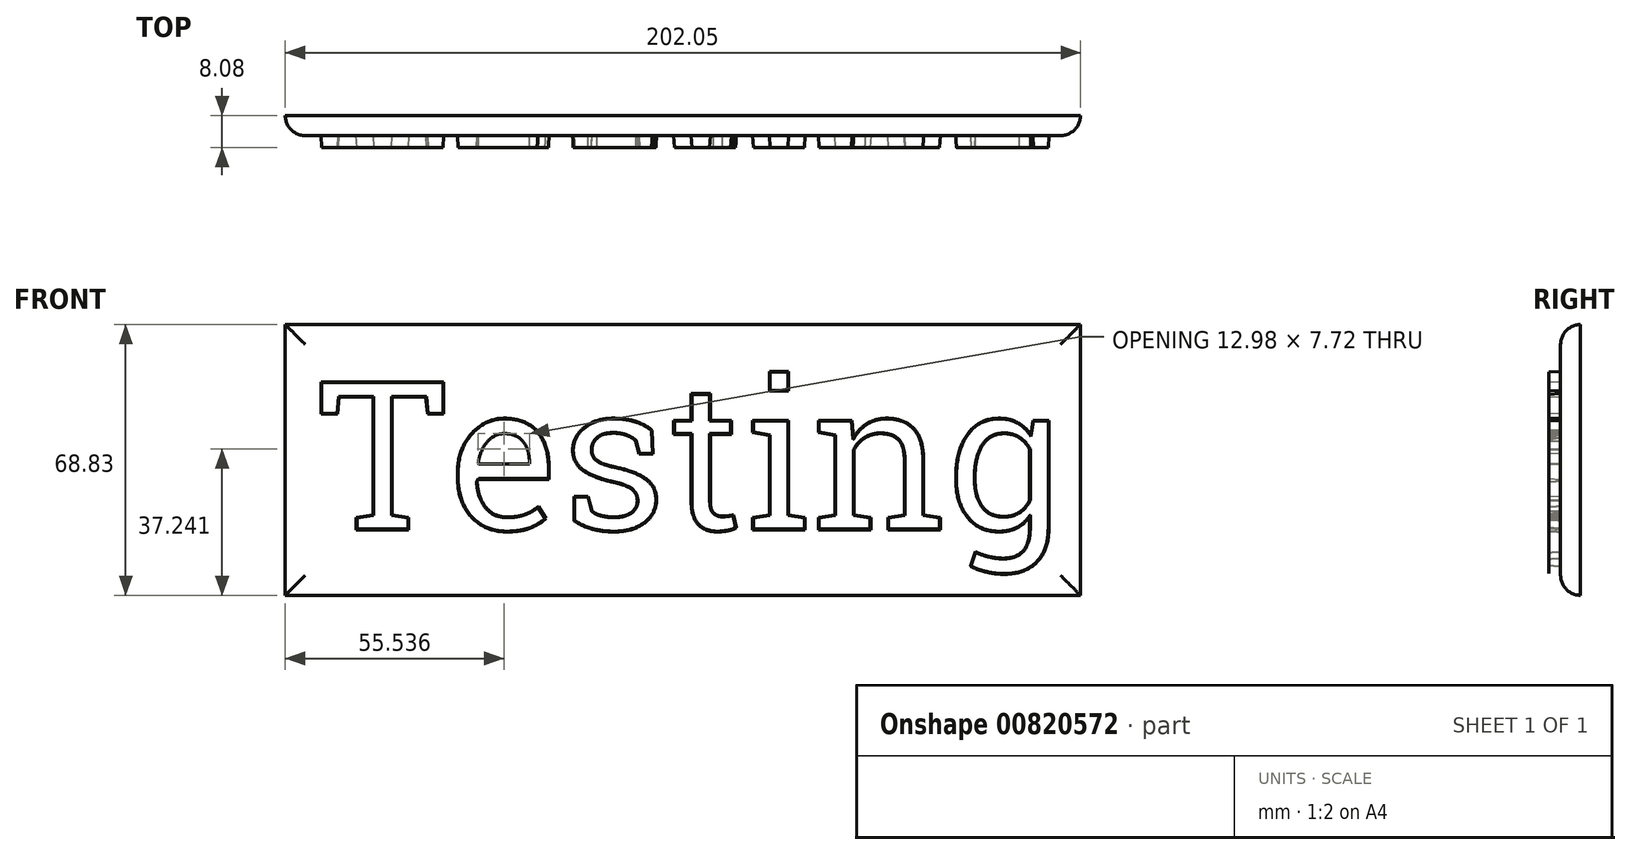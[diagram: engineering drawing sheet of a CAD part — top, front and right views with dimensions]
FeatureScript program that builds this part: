
annotation { "Feature Type Name" : "Feature", "Feature Type Description" : "" }
export const myFeature = defineFeature(function(context is Context, id is Id, definition is map)
    precondition{}
    {
        {
            var Q0;
            Q0=qCreatedBy(makeId("Front.planeOp"),FACE);
            var sketch = newSketch(context, id + "F0", { "sketchPlane" : qUnion([Q0])});
            skText(sketch, "E0", { "text": "Testing\n", "fontName": "RobotoSlab-Regular.ttf"});
            const initialGuessF0  = {"E0": [-0.06018, 0.01037, 1, 0, 0.0382]};
            skSetInitialGuess(sketch, initialGuessF0);
            skSolve(sketch);
        }
        {
            var Q0;
            Q0 = qSketchRegion(id + "F0", true);
            extrude(context, id + "F1", {"entities" : qUnion([Q0]), "depth" : 3 * mm, "offsetDistance" : 25.4 * mm});
        }
        {
            var Q0;
            Q0=qCreatedBy(makeId("Front.planeOp"),FACE);
            var sketch = newSketch(context, id + "F2", { "sketchPlane" : qUnion([Q0])});
            skLineSegment(sketch, "E1.bottom", {"start": v(-68.24, 62.63) * mm, "end": v(133.8, 62.63) * mm});
            skLineSegment(sketch, "E1.top", {"start": v(-68.24, -6.2) * mm, "end": v(133.8, -6.2) * mm});
            skLineSegment(sketch, "E1.left", {"start": v(-68.24, 62.63) * mm, "end": v(-68.24, -6.2) * mm});
            skLineSegment(sketch, "E1.right", {"start": v(133.8, 62.63) * mm, "end": v(133.8, -6.2) * mm});
            skSolve(sketch);
        }
        {
            var Q0;
            Q0 = qSketchRegion(id + "F2", true);
            extrude(context, id + "F3", {"entities" : qUnion([Q0]), "depth" : -5.08 * mm, "offsetDistance" : 25.4 * mm});
        }
        {
            var Q0;
            Q0=makeQuery(id+"F3.opExtrude","CAP_EDGE",EDGE,{"disambiguationData":[OSD([sQuery(id+"F2.wireOp",EDGE,"E1.left")])],"isStart":true});
            var Q1;
            Q1=makeQuery(id+"F3.opExtrude","CAP_EDGE",EDGE,{"disambiguationData":[OSD([sQuery(id+"F2.wireOp",EDGE,"E1.bottom")])],"isStart":true});
            var Q2;
            Q2=makeQuery(id+"F3.opExtrude","CAP_EDGE",EDGE,{"disambiguationData":[OSD([sQuery(id+"F2.wireOp",EDGE,"E1.right")])],"isStart":true});
            var Q3;
            Q3=makeQuery(id+"F3.opExtrude","CAP_EDGE",EDGE,{"disambiguationData":[OSD([sQuery(id+"F2.wireOp",EDGE,"E1.top")])],"isStart":true});
            chamfer(context, id + "F4", {"entities" : qUnion([Q0, Q1, Q2, Q3]), "chamferType" : ChamferType.OFFSET_ANGLE, "width" : 5.08 * mm, "oppositeDirection" : true, "angle" : 3 * degree, "tangentPropagation" : true});
        }
        {
            var Q0;
            Q0=makeQuery(id+"F1.opExtrude","CAP_EDGE",EDGE,{"disambiguationData":[OSD([sQuery(id+"F0.wireOp",EDGE,"E0.sketch_text.stroke-6")])],"isStart":false});
            var Q1;
            Q1=makeQuery(id+"F1.opExtrude","CAP_EDGE",EDGE,{"disambiguationData":[OSD([sQuery(id+"F0.wireOp",EDGE,"E0.sketch_text.stroke-7")])],"isStart":false});
            var Q2;
            Q2=makeQuery(id+"F1.opExtrude","CAP_EDGE",EDGE,{"disambiguationData":[OSD([sQuery(id+"F0.wireOp",EDGE,"E0.sketch_text.stroke-8")])],"isStart":false});
            var Q3;
            Q3=makeQuery(id+"F1.opExtrude","CAP_EDGE",EDGE,{"disambiguationData":[OSD([sQuery(id+"F0.wireOp",EDGE,"E0.sketch_text.stroke-9")])],"isStart":false});
            var Q4;
            Q4=makeQuery(id+"F1.opExtrude","CAP_EDGE",EDGE,{"disambiguationData":[OSD([sQuery(id+"F0.wireOp",EDGE,"E0.sketch_text.stroke-10")])],"isStart":false});
            var Q5;
            Q5=makeQuery(id+"F1.opExtrude","CAP_EDGE",EDGE,{"disambiguationData":[OSD([sQuery(id+"F0.wireOp",EDGE,"E0.sketch_text.stroke-5")])],"isStart":false});
            var Q6;
            Q6=makeQuery(id+"F1.opExtrude","CAP_EDGE",EDGE,{"disambiguationData":[OSD([sQuery(id+"F0.wireOp",EDGE,"E0.sketch_text.stroke-4")])],"isStart":false});
            var Q7;
            Q7=makeQuery(id+"F1.opExtrude","CAP_EDGE",EDGE,{"disambiguationData":[OSD([sQuery(id+"F0.wireOp",EDGE,"E0.sketch_text.stroke-3")])],"isStart":false});
            var Q8;
            Q8=makeQuery(id+"F1.opExtrude","CAP_EDGE",EDGE,{"disambiguationData":[OSD([sQuery(id+"F0.wireOp",EDGE,"E0.sketch_text.stroke-2")])],"isStart":false});
            var Q9;
            Q9=makeQuery(id+"F1.opExtrude","CAP_EDGE",EDGE,{"disambiguationData":[OSD([sQuery(id+"F0.wireOp",EDGE,"E0.sketch_text.stroke-1")])],"isStart":false});
            var Q10;
            Q10=makeQuery(id+"F1.opExtrude","CAP_EDGE",EDGE,{"disambiguationData":[OSD([sQuery(id+"F0.wireOp",EDGE,"E0.sketch_text.stroke-0")])],"isStart":false});
            var Q11;
            Q11=makeQuery(id+"F1.opExtrude","CAP_EDGE",EDGE,{"disambiguationData":[OSD([sQuery(id+"F0.wireOp",EDGE,"E0.sketch_text.stroke-15")])],"isStart":false});
            var Q12;
            Q12=makeQuery(id+"F1.opExtrude","CAP_EDGE",EDGE,{"disambiguationData":[OSD([sQuery(id+"F0.wireOp",EDGE,"E0.sketch_text.stroke-14")])],"isStart":false});
            var Q13;
            Q13=makeQuery(id+"F1.opExtrude","CAP_EDGE",EDGE,{"disambiguationData":[OSD([sQuery(id+"F0.wireOp",EDGE,"E0.sketch_text.stroke-13")])],"isStart":false});
            var Q14;
            Q14=makeQuery(id+"F1.opExtrude","CAP_EDGE",EDGE,{"disambiguationData":[OSD([sQuery(id+"F0.wireOp",EDGE,"E0.sketch_text.stroke-12")])],"isStart":false});
            var Q15;
            Q15=makeQuery(id+"F1.opExtrude","CAP_EDGE",EDGE,{"disambiguationData":[OSD([sQuery(id+"F0.wireOp",EDGE,"E0.sketch_text.stroke-11")])],"isStart":false});
            var Q16;
            Q16=makeQuery(id+"F1.opExtrude","CAP_EDGE",EDGE,{"disambiguationData":[OSD([sQuery(id+"F0.wireOp",EDGE,"E0.sketch_text.stroke-20")])],"isStart":false});
            var Q17;
            Q17=makeQuery(id+"F1.opExtrude","CAP_EDGE",EDGE,{"disambiguationData":[OSD([sQuery(id+"F0.wireOp",EDGE,"E0.sketch_text.stroke-21")])],"isStart":false});
            var Q18;
            Q18=makeQuery(id+"F1.opExtrude","CAP_EDGE",EDGE,{"disambiguationData":[OSD([sQuery(id+"F0.wireOp",EDGE,"E0.sketch_text.stroke-23")])],"isStart":false});
            var Q19;
            Q19=makeQuery(id+"F1.opExtrude","CAP_EDGE",EDGE,{"disambiguationData":[OSD([sQuery(id+"F0.wireOp",EDGE,"E0.sketch_text.stroke-24")])],"isStart":false});
            var Q20;
            Q20=makeQuery(id+"F1.opExtrude","CAP_EDGE",EDGE,{"disambiguationData":[OSD([sQuery(id+"F0.wireOp",EDGE,"E0.sketch_text.stroke-26")])],"isStart":false});
            var Q21;
            Q21=makeQuery(id+"F1.opExtrude","CAP_EDGE",EDGE,{"disambiguationData":[OSD([sQuery(id+"F0.wireOp",EDGE,"E0.sketch_text.stroke-27")])],"isStart":false});
            var Q22;
            Q22=makeQuery(id+"F1.opExtrude","CAP_EDGE",EDGE,{"disambiguationData":[OSD([sQuery(id+"F0.wireOp",EDGE,"E0.sketch_text.stroke-28")])],"isStart":false});
            var Q23;
            Q23=makeQuery(id+"F1.opExtrude","CAP_EDGE",EDGE,{"disambiguationData":[OSD([sQuery(id+"F0.wireOp",EDGE,"E0.sketch_text.stroke-29")])],"isStart":false});
            var Q24;
            Q24=makeQuery(id+"F1.opExtrude","CAP_EDGE",EDGE,{"disambiguationData":[OSD([sQuery(id+"F0.wireOp",EDGE,"E0.sketch_text.stroke-30")])],"isStart":false});
            var Q25;
            Q25=makeQuery(id+"F1.opExtrude","CAP_EDGE",EDGE,{"disambiguationData":[OSD([sQuery(id+"F0.wireOp",EDGE,"E0.sketch_text.stroke-31")])],"isStart":false});
            var Q26;
            Q26=makeQuery(id+"F1.opExtrude","CAP_EDGE",EDGE,{"disambiguationData":[OSD([sQuery(id+"F0.wireOp",EDGE,"E0.sketch_text.stroke-32")])],"isStart":false});
            var Q27;
            Q27=makeQuery(id+"F1.opExtrude","CAP_EDGE",EDGE,{"disambiguationData":[OSD([sQuery(id+"F0.wireOp",EDGE,"E0.sketch_text.stroke-16")])],"isStart":false});
            var Q28;
            Q28=makeQuery(id+"F1.opExtrude","CAP_EDGE",EDGE,{"disambiguationData":[OSD([sQuery(id+"F0.wireOp",EDGE,"E0.sketch_text.stroke-18")])],"isStart":false});
            var Q29;
            Q29=makeQuery(id+"F1.opExtrude","CAP_EDGE",EDGE,{"disambiguationData":[OSD([sQuery(id+"F0.wireOp",EDGE,"E0.sketch_text.stroke-17")])],"isStart":false});
            var Q30;
            Q30=makeQuery(id+"F1.opExtrude","CAP_EDGE",EDGE,{"disambiguationData":[OSD([sQuery(id+"F0.wireOp",EDGE,"E0.sketch_text.stroke-19")])],"isStart":false});
            var Q31;
            Q31=makeQuery(id+"F1.opExtrude","CAP_EDGE",EDGE,{"disambiguationData":[OSD([sQuery(id+"F0.wireOp",EDGE,"E0.sketch_text.stroke-55")])],"isStart":false});
            var Q32;
            Q32=makeQuery(id+"F1.opExtrude","CAP_EDGE",EDGE,{"disambiguationData":[OSD([sQuery(id+"F0.wireOp",EDGE,"E0.sketch_text.stroke-54")])],"isStart":false});
            var Q33;
            Q33=makeQuery(id+"F1.opExtrude","CAP_EDGE",EDGE,{"disambiguationData":[OSD([sQuery(id+"F0.wireOp",EDGE,"E0.sketch_text.stroke-53")])],"isStart":false});
            var Q34;
            Q34=makeQuery(id+"F1.opExtrude","CAP_EDGE",EDGE,{"disambiguationData":[OSD([sQuery(id+"F0.wireOp",EDGE,"E0.sketch_text.stroke-52")])],"isStart":false});
            var Q35;
            Q35=makeQuery(id+"F1.opExtrude","CAP_EDGE",EDGE,{"disambiguationData":[OSD([sQuery(id+"F0.wireOp",EDGE,"E0.sketch_text.stroke-51")])],"isStart":false});
            var Q36;
            Q36=makeQuery(id+"F1.opExtrude","CAP_EDGE",EDGE,{"disambiguationData":[OSD([sQuery(id+"F0.wireOp",EDGE,"E0.sketch_text.stroke-50")])],"isStart":false});
            var Q37;
            Q37=makeQuery(id+"F1.opExtrude","CAP_EDGE",EDGE,{"disambiguationData":[OSD([sQuery(id+"F0.wireOp",EDGE,"E0.sketch_text.stroke-49")])],"isStart":false});
            var Q38;
            Q38=makeQuery(id+"F1.opExtrude","CAP_EDGE",EDGE,{"disambiguationData":[OSD([sQuery(id+"F0.wireOp",EDGE,"E0.sketch_text.stroke-48")])],"isStart":false});
            var Q39;
            Q39=makeQuery(id+"F1.opExtrude","CAP_EDGE",EDGE,{"disambiguationData":[OSD([sQuery(id+"F0.wireOp",EDGE,"E0.sketch_text.stroke-47")])],"isStart":false});
            var Q40;
            Q40=makeQuery(id+"F1.opExtrude","CAP_EDGE",EDGE,{"disambiguationData":[OSD([sQuery(id+"F0.wireOp",EDGE,"E0.sketch_text.stroke-46")])],"isStart":false});
            var Q41;
            Q41=makeQuery(id+"F1.opExtrude","CAP_EDGE",EDGE,{"disambiguationData":[OSD([sQuery(id+"F0.wireOp",EDGE,"E0.sketch_text.stroke-45")])],"isStart":false});
            var Q42;
            Q42=makeQuery(id+"F1.opExtrude","CAP_EDGE",EDGE,{"disambiguationData":[OSD([sQuery(id+"F0.wireOp",EDGE,"E0.sketch_text.stroke-44")])],"isStart":false});
            var Q43;
            Q43=makeQuery(id+"F1.opExtrude","CAP_EDGE",EDGE,{"disambiguationData":[OSD([sQuery(id+"F0.wireOp",EDGE,"E0.sketch_text.stroke-43")])],"isStart":false});
            var Q44;
            Q44=makeQuery(id+"F1.opExtrude","CAP_EDGE",EDGE,{"disambiguationData":[OSD([sQuery(id+"F0.wireOp",EDGE,"E0.sketch_text.stroke-42")])],"isStart":false});
            var Q45;
            Q45=makeQuery(id+"F1.opExtrude","CAP_EDGE",EDGE,{"disambiguationData":[OSD([sQuery(id+"F0.wireOp",EDGE,"E0.sketch_text.stroke-41")])],"isStart":false});
            var Q46;
            Q46=makeQuery(id+"F1.opExtrude","CAP_EDGE",EDGE,{"disambiguationData":[OSD([sQuery(id+"F0.wireOp",EDGE,"E0.sketch_text.stroke-40")])],"isStart":false});
            var Q47;
            Q47=makeQuery(id+"F1.opExtrude","CAP_EDGE",EDGE,{"disambiguationData":[OSD([sQuery(id+"F0.wireOp",EDGE,"E0.sketch_text.stroke-69")])],"isStart":false});
            var Q48;
            Q48=makeQuery(id+"F1.opExtrude","CAP_EDGE",EDGE,{"disambiguationData":[OSD([sQuery(id+"F0.wireOp",EDGE,"E0.sketch_text.stroke-68")])],"isStart":false});
            var Q49;
            Q49=makeQuery(id+"F1.opExtrude","CAP_EDGE",EDGE,{"disambiguationData":[OSD([sQuery(id+"F0.wireOp",EDGE,"E0.sketch_text.stroke-67")])],"isStart":false});
            var Q50;
            Q50=makeQuery(id+"F1.opExtrude","CAP_EDGE",EDGE,{"disambiguationData":[OSD([sQuery(id+"F0.wireOp",EDGE,"E0.sketch_text.stroke-66")])],"isStart":false});
            var Q51;
            Q51=makeQuery(id+"F1.opExtrude","CAP_EDGE",EDGE,{"disambiguationData":[OSD([sQuery(id+"F0.wireOp",EDGE,"E0.sketch_text.stroke-65")])],"isStart":false});
            var Q52;
            Q52=makeQuery(id+"F1.opExtrude","CAP_EDGE",EDGE,{"disambiguationData":[OSD([sQuery(id+"F0.wireOp",EDGE,"E0.sketch_text.stroke-64")])],"isStart":false});
            var Q53;
            Q53=makeQuery(id+"F1.opExtrude","CAP_EDGE",EDGE,{"disambiguationData":[OSD([sQuery(id+"F0.wireOp",EDGE,"E0.sketch_text.stroke-63")])],"isStart":false});
            var Q54;
            Q54=makeQuery(id+"F1.opExtrude","CAP_EDGE",EDGE,{"disambiguationData":[OSD([sQuery(id+"F0.wireOp",EDGE,"E0.sketch_text.stroke-62")])],"isStart":false});
            var Q55;
            Q55=makeQuery(id+"F1.opExtrude","CAP_EDGE",EDGE,{"disambiguationData":[OSD([sQuery(id+"F0.wireOp",EDGE,"E0.sketch_text.stroke-61")])],"isStart":false});
            var Q56;
            Q56=makeQuery(id+"F1.opExtrude","CAP_EDGE",EDGE,{"disambiguationData":[OSD([sQuery(id+"F0.wireOp",EDGE,"E0.sketch_text.stroke-60")])],"isStart":false});
            var Q57;
            Q57=makeQuery(id+"F1.opExtrude","CAP_EDGE",EDGE,{"disambiguationData":[OSD([sQuery(id+"F0.wireOp",EDGE,"E0.sketch_text.stroke-59")])],"isStart":false});
            var Q58;
            Q58=makeQuery(id+"F1.opExtrude","CAP_EDGE",EDGE,{"disambiguationData":[OSD([sQuery(id+"F0.wireOp",EDGE,"E0.sketch_text.stroke-58")])],"isStart":false});
            var Q59;
            Q59=makeQuery(id+"F1.opExtrude","CAP_EDGE",EDGE,{"disambiguationData":[OSD([sQuery(id+"F0.wireOp",EDGE,"E0.sketch_text.stroke-57")])],"isStart":false});
            var Q60;
            Q60=makeQuery(id+"F1.opExtrude","CAP_EDGE",EDGE,{"disambiguationData":[OSD([sQuery(id+"F0.wireOp",EDGE,"E0.sketch_text.stroke-56")])],"isStart":false});
            var Q61;
            Q61=makeQuery(id+"F1.opExtrude","CAP_EDGE",EDGE,{"disambiguationData":[OSD([sQuery(id+"F0.wireOp",EDGE,"E0.sketch_text.stroke-89")])],"isStart":false});
            var Q62;
            Q62=makeQuery(id+"F1.opExtrude","CAP_EDGE",EDGE,{"disambiguationData":[OSD([sQuery(id+"F0.wireOp",EDGE,"E0.sketch_text.stroke-88")])],"isStart":false});
            var Q63;
            Q63=makeQuery(id+"F1.opExtrude","CAP_EDGE",EDGE,{"disambiguationData":[OSD([sQuery(id+"F0.wireOp",EDGE,"E0.sketch_text.stroke-87")])],"isStart":false});
            var Q64;
            Q64=makeQuery(id+"F1.opExtrude","CAP_EDGE",EDGE,{"disambiguationData":[OSD([sQuery(id+"F0.wireOp",EDGE,"E0.sketch_text.stroke-86")])],"isStart":false});
            var Q65;
            Q65=makeQuery(id+"F1.opExtrude","CAP_EDGE",EDGE,{"disambiguationData":[OSD([sQuery(id+"F0.wireOp",EDGE,"E0.sketch_text.stroke-85")])],"isStart":false});
            var Q66;
            Q66=makeQuery(id+"F1.opExtrude","CAP_EDGE",EDGE,{"disambiguationData":[OSD([sQuery(id+"F0.wireOp",EDGE,"E0.sketch_text.stroke-84")])],"isStart":false});
            var Q67;
            Q67=makeQuery(id+"F1.opExtrude","CAP_EDGE",EDGE,{"disambiguationData":[OSD([sQuery(id+"F0.wireOp",EDGE,"E0.sketch_text.stroke-70")])],"isStart":false});
            var Q68;
            Q68=makeQuery(id+"F1.opExtrude","CAP_EDGE",EDGE,{"disambiguationData":[OSD([sQuery(id+"F0.wireOp",EDGE,"E0.sketch_text.stroke-71")])],"isStart":false});
            var Q69;
            Q69=makeQuery(id+"F1.opExtrude","CAP_EDGE",EDGE,{"disambiguationData":[OSD([sQuery(id+"F0.wireOp",EDGE,"E0.sketch_text.stroke-72")])],"isStart":false});
            var Q70;
            Q70=makeQuery(id+"F1.opExtrude","CAP_EDGE",EDGE,{"disambiguationData":[OSD([sQuery(id+"F0.wireOp",EDGE,"E0.sketch_text.stroke-73")])],"isStart":false});
            var Q71;
            Q71=makeQuery(id+"F1.opExtrude","CAP_EDGE",EDGE,{"disambiguationData":[OSD([sQuery(id+"F0.wireOp",EDGE,"E0.sketch_text.stroke-74")])],"isStart":false});
            var Q72;
            Q72=makeQuery(id+"F1.opExtrude","CAP_EDGE",EDGE,{"disambiguationData":[OSD([sQuery(id+"F0.wireOp",EDGE,"E0.sketch_text.stroke-75")])],"isStart":false});
            var Q73;
            Q73=makeQuery(id+"F1.opExtrude","CAP_EDGE",EDGE,{"disambiguationData":[OSD([sQuery(id+"F0.wireOp",EDGE,"E0.sketch_text.stroke-76")])],"isStart":false});
            var Q74;
            Q74=makeQuery(id+"F1.opExtrude","CAP_EDGE",EDGE,{"disambiguationData":[OSD([sQuery(id+"F0.wireOp",EDGE,"E0.sketch_text.stroke-77")])],"isStart":false});
            var Q75;
            Q75=makeQuery(id+"F1.opExtrude","CAP_EDGE",EDGE,{"disambiguationData":[OSD([sQuery(id+"F0.wireOp",EDGE,"E0.sketch_text.stroke-78")])],"isStart":false});
            var Q76;
            Q76=makeQuery(id+"F1.opExtrude","CAP_EDGE",EDGE,{"disambiguationData":[OSD([sQuery(id+"F0.wireOp",EDGE,"E0.sketch_text.stroke-79")])],"isStart":false});
            var Q77;
            Q77=makeQuery(id+"F1.opExtrude","CAP_EDGE",EDGE,{"disambiguationData":[OSD([sQuery(id+"F0.wireOp",EDGE,"E0.sketch_text.stroke-83")])],"isStart":false});
            var Q78;
            Q78=makeQuery(id+"F1.opExtrude","CAP_EDGE",EDGE,{"disambiguationData":[OSD([sQuery(id+"F0.wireOp",EDGE,"E0.sketch_text.stroke-82")])],"isStart":false});
            var Q79;
            Q79=makeQuery(id+"F1.opExtrude","CAP_EDGE",EDGE,{"disambiguationData":[OSD([sQuery(id+"F0.wireOp",EDGE,"E0.sketch_text.stroke-81")])],"isStart":false});
            var Q80;
            Q80=makeQuery(id+"F1.opExtrude","CAP_EDGE",EDGE,{"disambiguationData":[OSD([sQuery(id+"F0.wireOp",EDGE,"E0.sketch_text.stroke-101")])],"isStart":false});
            var Q81;
            Q81=makeQuery(id+"F1.opExtrude","CAP_EDGE",EDGE,{"disambiguationData":[OSD([sQuery(id+"F0.wireOp",EDGE,"E0.sketch_text.stroke-102")])],"isStart":false});
            var Q82;
            Q82=makeQuery(id+"F1.opExtrude","CAP_EDGE",EDGE,{"disambiguationData":[OSD([sQuery(id+"F0.wireOp",EDGE,"E0.sketch_text.stroke-103")])],"isStart":false});
            var Q83;
            Q83=makeQuery(id+"F1.opExtrude","CAP_EDGE",EDGE,{"disambiguationData":[OSD([sQuery(id+"F0.wireOp",EDGE,"E0.sketch_text.stroke-100")])],"isStart":false});
            var Q84;
            Q84=makeQuery(id+"F1.opExtrude","CAP_EDGE",EDGE,{"disambiguationData":[OSD([sQuery(id+"F0.wireOp",EDGE,"E0.sketch_text.stroke-94")])],"isStart":false});
            var Q85;
            Q85=makeQuery(id+"F1.opExtrude","CAP_EDGE",EDGE,{"disambiguationData":[OSD([sQuery(id+"F0.wireOp",EDGE,"E0.sketch_text.stroke-93")])],"isStart":false});
            var Q86;
            Q86=makeQuery(id+"F1.opExtrude","CAP_EDGE",EDGE,{"disambiguationData":[OSD([sQuery(id+"F0.wireOp",EDGE,"E0.sketch_text.stroke-92")])],"isStart":false});
            var Q87;
            Q87=makeQuery(id+"F1.opExtrude","CAP_EDGE",EDGE,{"disambiguationData":[OSD([sQuery(id+"F0.wireOp",EDGE,"E0.sketch_text.stroke-91")])],"isStart":false});
            var Q88;
            Q88=makeQuery(id+"F1.opExtrude","CAP_EDGE",EDGE,{"disambiguationData":[OSD([sQuery(id+"F0.wireOp",EDGE,"E0.sketch_text.stroke-90")])],"isStart":false});
            var Q89;
            Q89=makeQuery(id+"F1.opExtrude","CAP_EDGE",EDGE,{"disambiguationData":[OSD([sQuery(id+"F0.wireOp",EDGE,"E0.sketch_text.stroke-99")])],"isStart":false});
            var Q90;
            Q90=makeQuery(id+"F1.opExtrude","CAP_EDGE",EDGE,{"disambiguationData":[OSD([sQuery(id+"F0.wireOp",EDGE,"E0.sketch_text.stroke-98")])],"isStart":false});
            var Q91;
            Q91=makeQuery(id+"F1.opExtrude","CAP_EDGE",EDGE,{"disambiguationData":[OSD([sQuery(id+"F0.wireOp",EDGE,"E0.sketch_text.stroke-97")])],"isStart":false});
            var Q92;
            Q92=makeQuery(id+"F1.opExtrude","CAP_EDGE",EDGE,{"disambiguationData":[OSD([sQuery(id+"F0.wireOp",EDGE,"E0.sketch_text.stroke-96")])],"isStart":false});
            var Q93;
            Q93=makeQuery(id+"F1.opExtrude","CAP_EDGE",EDGE,{"disambiguationData":[OSD([sQuery(id+"F0.wireOp",EDGE,"E0.sketch_text.stroke-95")])],"isStart":false});
            var Q94;
            Q94=makeQuery(id+"F1.opExtrude","CAP_EDGE",EDGE,{"disambiguationData":[OSD([sQuery(id+"F0.wireOp",EDGE,"E0.sketch_text.stroke-80")])],"isStart":false});
            var Q95;
            Q95=makeQuery(id+"F1.opExtrude","CAP_EDGE",EDGE,{"disambiguationData":[OSD([sQuery(id+"F0.wireOp",EDGE,"E0.sketch_text.stroke-107")])],"isStart":false});
            var Q96;
            Q96=makeQuery(id+"F1.opExtrude","CAP_EDGE",EDGE,{"disambiguationData":[OSD([sQuery(id+"F0.wireOp",EDGE,"E0.sketch_text.stroke-108")])],"isStart":false});
            var Q97;
            Q97=makeQuery(id+"F1.opExtrude","CAP_EDGE",EDGE,{"disambiguationData":[OSD([sQuery(id+"F0.wireOp",EDGE,"E0.sketch_text.stroke-109")])],"isStart":false});
            var Q98;
            Q98=makeQuery(id+"F1.opExtrude","CAP_EDGE",EDGE,{"disambiguationData":[OSD([sQuery(id+"F0.wireOp",EDGE,"E0.sketch_text.stroke-106")])],"isStart":false});
            var Q99;
            Q99=makeQuery(id+"F1.opExtrude","CAP_EDGE",EDGE,{"disambiguationData":[OSD([sQuery(id+"F0.wireOp",EDGE,"E0.sketch_text.stroke-105")])],"isStart":false});
            var Q100;
            Q100=makeQuery(id+"F1.opExtrude","CAP_EDGE",EDGE,{"disambiguationData":[OSD([sQuery(id+"F0.wireOp",EDGE,"E0.sketch_text.stroke-104")])],"isStart":false});
            var Q101;
            Q101=makeQuery(id+"F1.opExtrude","CAP_EDGE",EDGE,{"disambiguationData":[OSD([sQuery(id+"F0.wireOp",EDGE,"E0.sketch_text.stroke-129")])],"isStart":false});
            var Q102;
            Q102=makeQuery(id+"F1.opExtrude","CAP_EDGE",EDGE,{"disambiguationData":[OSD([sQuery(id+"F0.wireOp",EDGE,"E0.sketch_text.stroke-22")])],"isStart":false});
            var Q103;
            Q103=makeQuery(id+"F1.opExtrude","CAP_EDGE",EDGE,{"disambiguationData":[OSD([sQuery(id+"F0.wireOp",EDGE,"E0.sketch_text.stroke-128")])],"isStart":false});
            var Q104;
            Q104=makeQuery(id+"F1.opExtrude","CAP_EDGE",EDGE,{"disambiguationData":[OSD([sQuery(id+"F0.wireOp",EDGE,"E0.sketch_text.stroke-127")])],"isStart":false});
            var Q105;
            Q105=makeQuery(id+"F1.opExtrude","CAP_EDGE",EDGE,{"disambiguationData":[OSD([sQuery(id+"F0.wireOp",EDGE,"E0.sketch_text.stroke-126")])],"isStart":false});
            var Q106;
            Q106=makeQuery(id+"F1.opExtrude","CAP_EDGE",EDGE,{"disambiguationData":[OSD([sQuery(id+"F0.wireOp",EDGE,"E0.sketch_text.stroke-125")])],"isStart":false});
            var Q107;
            Q107=makeQuery(id+"F1.opExtrude","CAP_EDGE",EDGE,{"disambiguationData":[OSD([sQuery(id+"F0.wireOp",EDGE,"E0.sketch_text.stroke-110")])],"isStart":false});
            var Q108;
            Q108=makeQuery(id+"F1.opExtrude","CAP_EDGE",EDGE,{"disambiguationData":[OSD([sQuery(id+"F0.wireOp",EDGE,"E0.sketch_text.stroke-111")])],"isStart":false});
            var Q109;
            Q109=makeQuery(id+"F1.opExtrude","CAP_EDGE",EDGE,{"disambiguationData":[OSD([sQuery(id+"F0.wireOp",EDGE,"E0.sketch_text.stroke-124")])],"isStart":false});
            var Q110;
            Q110=makeQuery(id+"F1.opExtrude","CAP_EDGE",EDGE,{"disambiguationData":[OSD([sQuery(id+"F0.wireOp",EDGE,"E0.sketch_text.stroke-112")])],"isStart":false});
            var Q111;
            Q111=makeQuery(id+"F1.opExtrude","CAP_EDGE",EDGE,{"disambiguationData":[OSD([sQuery(id+"F0.wireOp",EDGE,"E0.sketch_text.stroke-113")])],"isStart":false});
            var Q112;
            Q112=makeQuery(id+"F1.opExtrude","CAP_EDGE",EDGE,{"disambiguationData":[OSD([sQuery(id+"F0.wireOp",EDGE,"E0.sketch_text.stroke-114")])],"isStart":false});
            var Q113;
            Q113=makeQuery(id+"F1.opExtrude","CAP_EDGE",EDGE,{"disambiguationData":[OSD([sQuery(id+"F0.wireOp",EDGE,"E0.sketch_text.stroke-115")])],"isStart":false});
            var Q114;
            Q114=makeQuery(id+"F1.opExtrude","CAP_EDGE",EDGE,{"disambiguationData":[OSD([sQuery(id+"F0.wireOp",EDGE,"E0.sketch_text.stroke-116")])],"isStart":false});
            var Q115;
            Q115=makeQuery(id+"F1.opExtrude","CAP_EDGE",EDGE,{"disambiguationData":[OSD([sQuery(id+"F0.wireOp",EDGE,"E0.sketch_text.stroke-117")])],"isStart":false});
            var Q116;
            Q116=makeQuery(id+"F1.opExtrude","CAP_EDGE",EDGE,{"disambiguationData":[OSD([sQuery(id+"F0.wireOp",EDGE,"E0.sketch_text.stroke-118")])],"isStart":false});
            var Q117;
            Q117=makeQuery(id+"F1.opExtrude","CAP_EDGE",EDGE,{"disambiguationData":[OSD([sQuery(id+"F0.wireOp",EDGE,"E0.sketch_text.stroke-119")])],"isStart":false});
            var Q118;
            Q118=makeQuery(id+"F1.opExtrude","CAP_EDGE",EDGE,{"disambiguationData":[OSD([sQuery(id+"F0.wireOp",EDGE,"E0.sketch_text.stroke-120")])],"isStart":false});
            var Q119;
            Q119=makeQuery(id+"F1.opExtrude","CAP_EDGE",EDGE,{"disambiguationData":[OSD([sQuery(id+"F0.wireOp",EDGE,"E0.sketch_text.stroke-123")])],"isStart":false});
            var Q120;
            Q120=makeQuery(id+"F1.opExtrude","CAP_EDGE",EDGE,{"disambiguationData":[OSD([sQuery(id+"F0.wireOp",EDGE,"E0.sketch_text.stroke-121")])],"isStart":false});
            var Q121;
            Q121=makeQuery(id+"F1.opExtrude","CAP_EDGE",EDGE,{"disambiguationData":[OSD([sQuery(id+"F0.wireOp",EDGE,"E0.sketch_text.stroke-122")])],"isStart":false});
            chamfer(context, id + "F5", {"entities" : qUnion([Q0, Q1, Q2, Q3, Q4, Q5, Q6, Q7, Q8, Q9, Q10, Q11, Q12, Q13, Q14, Q15, Q16, Q17, Q18, Q19, Q20, Q21, Q22, Q23, Q24, Q25, Q26, Q27, Q28, Q29, Q30, Q31, Q32, Q33, Q34, Q35, Q36, Q37, Q38, Q39, Q40, Q41, Q42, Q43, Q44, Q45, Q46, Q47, Q48, Q49, Q50, Q51, Q52, Q53, Q54, Q55, Q56, Q57, Q58, Q59, Q60, Q61, Q62, Q63, Q64, Q65, Q66, Q67, Q68, Q69, Q70, Q71, Q72, Q73, Q74, Q75, Q76, Q77, Q78, Q79, Q80, Q81, Q82, Q83, Q84, Q85, Q86, Q87, Q88, Q89, Q90, Q91, Q92, Q93, Q94, Q95, Q96, Q97, Q98, Q99, Q100, Q101, Q102, Q103, Q104, Q105, Q106, Q107, Q108, Q109, Q110, Q111, Q112, Q113, Q114, Q115, Q116, Q117, Q118, Q119, Q120, Q121]), "chamferType" : ChamferType.OFFSET_ANGLE, "width" : 5.08 * mm, "oppositeDirection" : false, "angle" : 3 * degree, "tangentPropagation" : true});
        }
        {
            var Q0;
            Q0=makeQuery(id+"F1.opExtrude","CAP_FACE",FACE,{"disambiguationData":[OSD([sQuery(id+"F0.wireOp",EDGE,"E0.sketch_text.stroke-130"),sQuery(id+"F0.wireOp",EDGE,"E0.sketch_text.stroke-131"),sQuery(id+"F0.wireOp",EDGE,"E0.sketch_text.stroke-132"),sQuery(id+"F0.wireOp",EDGE,"E0.sketch_text.stroke-133"),sQuery(id+"F0.wireOp",EDGE,"E0.sketch_text.stroke-134"),sQuery(id+"F0.wireOp",EDGE,"E0.sketch_text.stroke-135"),sQuery(id+"F0.wireOp",EDGE,"E0.sketch_text.stroke-136"),sQuery(id+"F0.wireOp",EDGE,"E0.sketch_text.stroke-137"),sQuery(id+"F0.wireOp",EDGE,"E0.sketch_text.stroke-138"),sQuery(id+"F0.wireOp",EDGE,"E0.sketch_text.stroke-139"),sQuery(id+"F0.wireOp",EDGE,"E0.sketch_text.stroke-140"),sQuery(id+"F0.wireOp",EDGE,"E0.sketch_text.stroke-141"),sQuery(id+"F0.wireOp",EDGE,"E0.sketch_text.stroke-142"),sQuery(id+"F0.wireOp",EDGE,"E0.sketch_text.stroke-143"),sQuery(id+"F0.wireOp",EDGE,"E0.sketch_text.stroke-144"),sQuery(id+"F0.wireOp",EDGE,"E0.sketch_text.stroke-145"),sQuery(id+"F0.wireOp",EDGE,"E0.sketch_text.stroke-146"),sQuery(id+"F0.wireOp",EDGE,"E0.sketch_text.stroke-147"),sQuery(id+"F0.wireOp",EDGE,"E0.sketch_text.stroke-148"),sQuery(id+"F0.wireOp",EDGE,"E0.sketch_text.stroke-149"),sQuery(id+"F0.wireOp",EDGE,"E0.sketch_text.stroke-150"),sQuery(id+"F0.wireOp",EDGE,"E0.sketch_text.stroke-151"),sQuery(id+"F0.wireOp",EDGE,"E0.sketch_text.stroke-152"),sQuery(id+"F0.wireOp",EDGE,"E0.sketch_text.stroke-153"),sQuery(id+"F0.wireOp",EDGE,"E0.sketch_text.stroke-154"),sQuery(id+"F0.wireOp",EDGE,"E0.sketch_text.stroke-155"),sQuery(id+"F0.wireOp",EDGE,"E0.sketch_text.stroke-156"),sQuery(id+"F0.wireOp",EDGE,"E0.sketch_text.stroke-157"),sQuery(id+"F0.wireOp",EDGE,"E0.sketch_text.stroke-158"),sQuery(id+"F0.wireOp",EDGE,"E0.sketch_text.stroke-159"),sQuery(id+"F0.wireOp",EDGE,"E0.sketch_text.stroke-160"),sQuery(id+"F0.wireOp",EDGE,"E0.sketch_text.stroke-161")])],"isStart":false});
            chamfer(context, id + "F6", {"entities" : qUnion([Q0]), "chamferType" : ChamferType.OFFSET_ANGLE, "width" : 5.08 * mm, "oppositeDirection" : false, "angle" : 3 * degree, "tangentPropagation" : true});
        }
        {
            var Q0;
            {var subQ0=sQuery(id+"F2.wireOp",EDGE,"E1.bottom");Q0=makeQuery(id+"F4.opChamfer","BLEND_EDGE",EDGE,{"blendedFrom":[makeQuery(id+"F3.opExtrude","CAP_EDGE",EDGE,{"disambiguationData":[OSD([subQ0])],"isStart":true}),makeQuery(id+"F3.opExtrude","CAP_FACE",FACE,{"disambiguationData":[OSD([subQ0,sQuery(id+"F2.wireOp",EDGE,"E1.top"),sQuery(id+"F2.wireOp",EDGE,"E1.left"),sQuery(id+"F2.wireOp",EDGE,"E1.right")])],"isStart":true})],"blendedInto":[makeQuery(id+"F3.opExtrude","CAP_FACE",FACE,{"disambiguationData":[OSD([subQ0,sQuery(id+"F2.wireOp",EDGE,"E1.top"),sQuery(id+"F2.wireOp",EDGE,"E1.left"),sQuery(id+"F2.wireOp",EDGE,"E1.right")])],"isStart":true})]});}
            var Q1;
            {var subQ0=sQuery(id+"F2.wireOp",EDGE,"E1.left");Q1=makeQuery(id+"F4.opChamfer","BLEND_EDGE",EDGE,{"blendedFrom":[makeQuery(id+"F3.opExtrude","CAP_EDGE",EDGE,{"disambiguationData":[OSD([subQ0])],"isStart":true}),makeQuery(id+"F3.opExtrude","CAP_FACE",FACE,{"disambiguationData":[OSD([sQuery(id+"F2.wireOp",EDGE,"E1.bottom"),sQuery(id+"F2.wireOp",EDGE,"E1.top"),subQ0,sQuery(id+"F2.wireOp",EDGE,"E1.right")])],"isStart":true})],"blendedInto":[makeQuery(id+"F3.opExtrude","CAP_FACE",FACE,{"disambiguationData":[OSD([sQuery(id+"F2.wireOp",EDGE,"E1.bottom"),sQuery(id+"F2.wireOp",EDGE,"E1.top"),subQ0,sQuery(id+"F2.wireOp",EDGE,"E1.right")])],"isStart":true})]});}
            var Q2;
            {var subQ0=sQuery(id+"F2.wireOp",EDGE,"E1.top");Q2=makeQuery(id+"F4.opChamfer","BLEND_EDGE",EDGE,{"blendedFrom":[makeQuery(id+"F3.opExtrude","CAP_EDGE",EDGE,{"disambiguationData":[OSD([subQ0])],"isStart":true}),makeQuery(id+"F3.opExtrude","CAP_FACE",FACE,{"disambiguationData":[OSD([sQuery(id+"F2.wireOp",EDGE,"E1.bottom"),subQ0,sQuery(id+"F2.wireOp",EDGE,"E1.left"),sQuery(id+"F2.wireOp",EDGE,"E1.right")])],"isStart":true})],"blendedInto":[makeQuery(id+"F3.opExtrude","CAP_FACE",FACE,{"disambiguationData":[OSD([sQuery(id+"F2.wireOp",EDGE,"E1.bottom"),subQ0,sQuery(id+"F2.wireOp",EDGE,"E1.left"),sQuery(id+"F2.wireOp",EDGE,"E1.right")])],"isStart":true})]});}
            var Q3;
            {var subQ0=sQuery(id+"F2.wireOp",EDGE,"E1.right");Q3=makeQuery(id+"F4.opChamfer","BLEND_EDGE",EDGE,{"blendedFrom":[makeQuery(id+"F3.opExtrude","CAP_EDGE",EDGE,{"disambiguationData":[OSD([subQ0])],"isStart":true}),makeQuery(id+"F3.opExtrude","CAP_FACE",FACE,{"disambiguationData":[OSD([sQuery(id+"F2.wireOp",EDGE,"E1.bottom"),sQuery(id+"F2.wireOp",EDGE,"E1.top"),sQuery(id+"F2.wireOp",EDGE,"E1.left"),subQ0])],"isStart":true})],"blendedInto":[makeQuery(id+"F3.opExtrude","CAP_FACE",FACE,{"disambiguationData":[OSD([sQuery(id+"F2.wireOp",EDGE,"E1.bottom"),sQuery(id+"F2.wireOp",EDGE,"E1.top"),sQuery(id+"F2.wireOp",EDGE,"E1.left"),subQ0])],"isStart":true})]});}
            fillet(context, id + "F7", {"entities" : qUnion([Q0, Q1, Q2, Q3]), "radius" : 5.08 * mm, "tangentPropagation" : true, "allowEdgeOverflow" : false});
        }
    });
